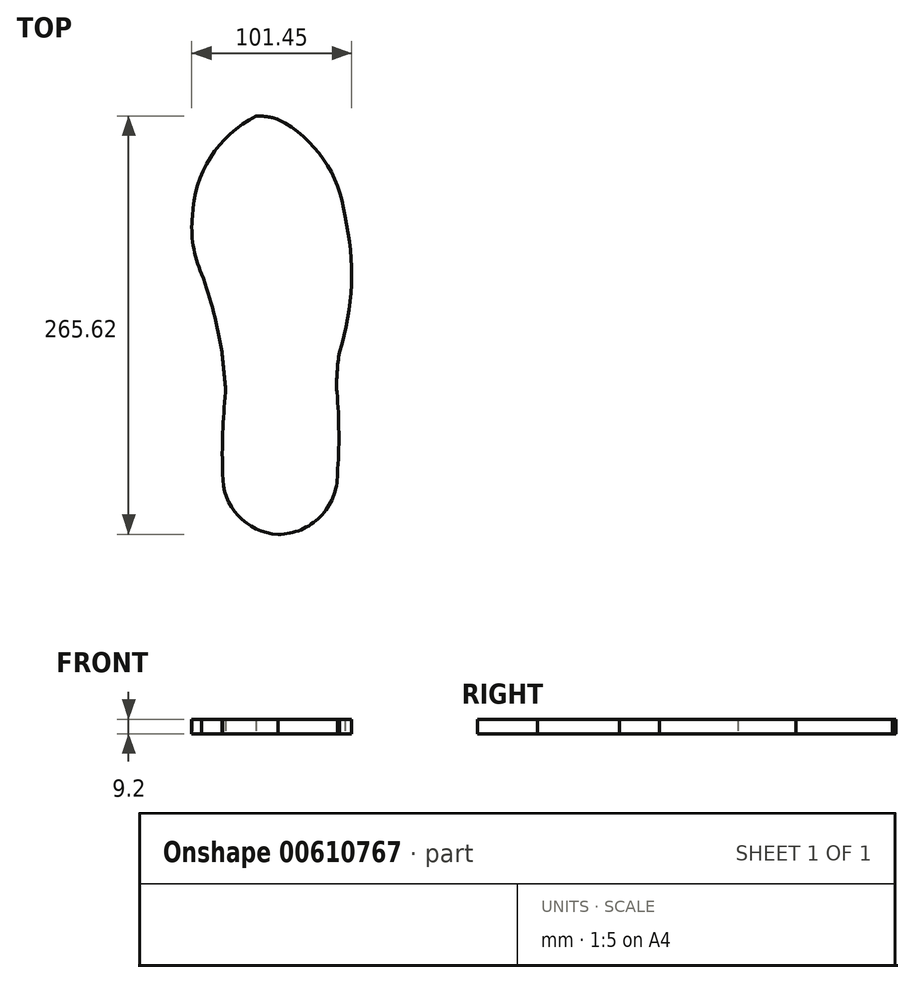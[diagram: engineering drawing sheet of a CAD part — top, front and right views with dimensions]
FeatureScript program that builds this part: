
annotation { "Feature Type Name" : "Feature", "Feature Type Description" : "" }
export const myFeature = defineFeature(function(context is Context, id is Id, definition is map)
    precondition{}
    {
        {
            var Q0;
            Q0=qCreatedBy(makeId("Top.planeOp"),FACE);
            var sketch = newSketch(context, id + "F0", { "sketchPlane" : qUnion([Q0])});
            skArc(sketch, "E0", {"start": v(42.33, 202.17) * mm, "mid": v(28.84, 238.17) * mm, "end": v(0, 263.58) * mm});
            skArc(sketch, "E1", {"start": v(0, 263.58) * mm, "mid": v(-7, 265.24) * mm, "end": v(-14.17, 265.57) * mm});
            skArc(sketch, "E2", {"start": v(-14.17, 265.57) * mm, "mid": v(-43, 239.38) * mm, "end": v(-54.5, 202.17) * mm});
            skArc(sketch, "E3", {"start": v(-35.72, 115.73) * mm, "mid": v(-40.92, 140.86) * mm, "end": v(-48.55, 165.36) * mm});
            skArc(sketch, "E4", {"start": v(-54.5, 202.17) * mm, "mid": v(-53.94, 183.38) * mm, "end": v(-48.55, 165.36) * mm});
            skArc(sketch, "E5", {"start": v(-33.26, 90.32) * mm, "mid": v(-34.44, 103.03) * mm, "end": v(-35.72, 115.73) * mm});
            skArc(sketch, "E6", {"start": v(-33.26, 90.32) * mm, "mid": v(-35.25, 64.29) * mm, "end": v(-35.21, 38.17) * mm});
            skArc(sketch, "E7", {"start": v(-35.21, 38.17) * mm, "mid": v(-25.46, 11.85) * mm, "end": v(0, 0) * mm});
            skArc(sketch, "E8", {"start": v(0, 0) * mm, "mid": v(26.8, 11.2) * mm, "end": v(37.57, 38.17) * mm});
            skArc(sketch, "E9", {"start": v(37.57, 38.17) * mm, "mid": v(38.54, 64.25) * mm, "end": v(37.3, 90.32) * mm});
            skArc(sketch, "E10", {"start": v(39.02, 115.73) * mm, "mid": v(37.44, 103.07) * mm, "end": v(37.3, 90.32) * mm});
            skArc(sketch, "E11", {"start": v(39.02, 115.73) * mm, "mid": v(46.46, 158.73) * mm, "end": v(42.33, 202.17) * mm});
            skPoint(sketch, "E12.end.orphan", {"position": v(0, 165.36) * mm});
            skPoint(sketch, "E13.orphan", {"position": v(0, 38.17) * mm});
            skPoint(sketch, "E14.start.orphan", {"position": v(0, 260) * mm});
            skSolve(sketch);
        }
        {
            var Q0;
            Q0=makeQuery(id+"F0.imprint","IMPRINT",FACE,{"disambiguationData":[TD([[makeQuery(id+"F0.imprint","IMPRINT",EDGE,{"derivedFrom":sQuery(id+"F0.wireOp",EDGE,"E0")}),1.0]])]});
            extrude(context, id + "F1", {"entities" : qUnion([Q0]), "depth" : 9.2 * mm, "offsetDistance" : 25 * mm});
        }
    });
